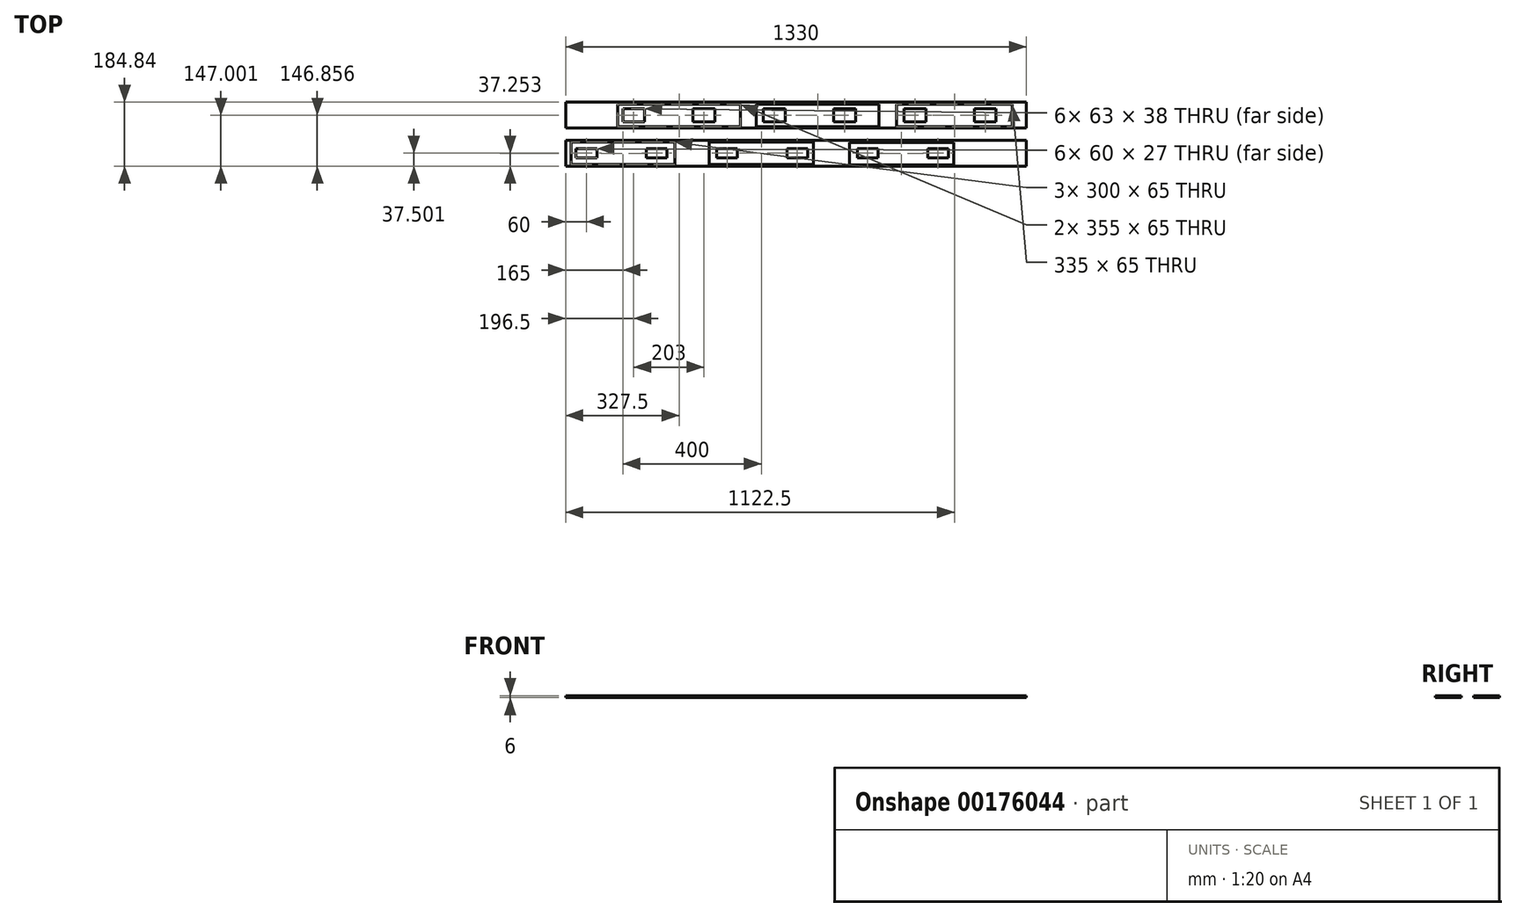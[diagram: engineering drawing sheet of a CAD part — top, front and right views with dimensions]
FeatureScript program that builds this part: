
annotation { "Feature Type Name" : "Feature", "Feature Type Description" : "" }
export const myFeature = defineFeature(function(context is Context, id is Id, definition is map)
    precondition{}
    {
        {
            var Q0;
            Q0=qCreatedBy(makeId("Top.planeOp"),FACE);
            var sketch = newSketch(context, id + "F0", { "sketchPlane" : qUnion([Q0])});
            skLineSegment(sketch, "E0.bottom", {"start": v(0, 0) * mm, "end": v(1330, 0) * mm});
            skLineSegment(sketch, "E0.top", {"start": v(0, 75) * mm, "end": v(1330, 75) * mm});
            skLineSegment(sketch, "E0.left", {"start": v(0, 0) * mm, "end": v(0, 75) * mm});
            skLineSegment(sketch, "E0.right", {"start": v(1330, 0) * mm, "end": v(1330, 75) * mm});
            skLineSegment(sketch, "E1.bottom", {"start": v(0, -34.84) * mm, "end": v(1330, -34.84) * mm});
            skLineSegment(sketch, "E1.top", {"start": v(0, -109.84) * mm, "end": v(1330, -109.84) * mm});
            skLineSegment(sketch, "E1.left", {"start": v(0, -34.84) * mm, "end": v(0, -109.84) * mm});
            skLineSegment(sketch, "E1.right", {"start": v(1330, -34.84) * mm, "end": v(1330, -109.84) * mm});
            skLineSegment(sketch, "E2.bottom", {"start": v(15, -40.09) * mm, "end": v(315, -40.09) * mm});
            skLineSegment(sketch, "E2.top", {"start": v(15, -105.09) * mm, "end": v(315, -105.09) * mm});
            skLineSegment(sketch, "E2.left", {"start": v(15, -40.09) * mm, "end": v(15, -105.09) * mm});
            skLineSegment(sketch, "E2.right", {"start": v(315, -40.09) * mm, "end": v(315, -105.09) * mm});
            skLineSegment(sketch, "E3.bottom", {"start": v(415, -39.91) * mm, "end": v(715, -39.91) * mm});
            skLineSegment(sketch, "E3.top", {"start": v(415, -104.91) * mm, "end": v(715, -104.91) * mm});
            skLineSegment(sketch, "E3.left", {"start": v(415, -39.91) * mm, "end": v(415, -104.91) * mm});
            skLineSegment(sketch, "E3.right", {"start": v(715, -39.91) * mm, "end": v(715, -104.91) * mm});
            skLineSegment(sketch, "E4.bottom", {"start": v(820, -40.85) * mm, "end": v(1120, -40.85) * mm});
            skLineSegment(sketch, "E4.top", {"start": v(820, -105.85) * mm, "end": v(1120, -105.85) * mm});
            skLineSegment(sketch, "E4.left", {"start": v(820, -40.85) * mm, "end": v(820, -105.85) * mm});
            skLineSegment(sketch, "E4.right", {"start": v(1120, -40.85) * mm, "end": v(1120, -105.85) * mm});
            skLineSegment(sketch, "E5.bottom", {"start": v(150, 69.52) * mm, "end": v(505, 69.52) * mm});
            skLineSegment(sketch, "E5.top", {"start": v(150, 4.52) * mm, "end": v(505, 4.52) * mm});
            skLineSegment(sketch, "E5.left", {"start": v(150, 69.52) * mm, "end": v(150, 4.52) * mm});
            skLineSegment(sketch, "E5.right", {"start": v(505, 69.52) * mm, "end": v(505, 4.52) * mm});
            skLineSegment(sketch, "E6.bottom", {"start": v(550, 69.52) * mm, "end": v(905, 69.52) * mm});
            skLineSegment(sketch, "E6.top", {"start": v(550, 4.52) * mm, "end": v(905, 4.52) * mm});
            skLineSegment(sketch, "E6.left", {"start": v(550, 69.52) * mm, "end": v(550, 4.52) * mm});
            skLineSegment(sketch, "E6.right", {"start": v(905, 69.52) * mm, "end": v(905, 4.52) * mm});
            skLineSegment(sketch, "E7.bottom", {"start": v(955, 69.52) * mm, "end": v(1290, 69.52) * mm});
            skLineSegment(sketch, "E7.top", {"start": v(955, 4.52) * mm, "end": v(1290, 4.52) * mm});
            skLineSegment(sketch, "E7.left", {"start": v(955, 69.52) * mm, "end": v(955, 4.52) * mm});
            skLineSegment(sketch, "E7.right", {"start": v(1290, 69.52) * mm, "end": v(1290, 4.52) * mm});
            skSolve(sketch);
        }
        {
            var Q0;
            Q0=qCreatedBy(makeId("Top.planeOp"),FACE);
            var sketch = newSketch(context, id + "F1", { "sketchPlane" : qUnion([Q0])});
            skLineSegment(sketch, "E8.bottom", {"start": v(165, 56.16) * mm, "end": v(228, 56.16) * mm});
            skLineSegment(sketch, "E8.top", {"start": v(165, 18.16) * mm, "end": v(228, 18.16) * mm});
            skLineSegment(sketch, "E8.left", {"start": v(165, 56.16) * mm, "end": v(165, 18.16) * mm});
            skLineSegment(sketch, "E8.right", {"start": v(228, 56.16) * mm, "end": v(228, 18.16) * mm});
            skLineSegment(sketch, "E9.bottom", {"start": v(30, -58.84) * mm, "end": v(90, -58.84) * mm});
            skLineSegment(sketch, "E9.top", {"start": v(30, -85.84) * mm, "end": v(90, -85.84) * mm});
            skLineSegment(sketch, "E9.left", {"start": v(30, -58.84) * mm, "end": v(30, -85.84) * mm});
            skLineSegment(sketch, "E9.right", {"start": v(90, -58.84) * mm, "end": v(90, -85.84) * mm});
            skLineSegment(sketch, "E10.bottom", {"start": v(368, 56.16) * mm, "end": v(431, 56.16) * mm});
            skLineSegment(sketch, "E10.top", {"start": v(368, 18.16) * mm, "end": v(431, 18.16) * mm});
            skLineSegment(sketch, "E10.left", {"start": v(368, 56.16) * mm, "end": v(368, 18.16) * mm});
            skLineSegment(sketch, "E10.right", {"start": v(431, 56.16) * mm, "end": v(431, 18.16) * mm});
            skLineSegment(sketch, "E11.bottom", {"start": v(233, -58.84) * mm, "end": v(293, -58.84) * mm});
            skLineSegment(sketch, "E11.top", {"start": v(233, -85.84) * mm, "end": v(293, -85.84) * mm});
            skLineSegment(sketch, "E11.left", {"start": v(233, -58.84) * mm, "end": v(233, -85.84) * mm});
            skLineSegment(sketch, "E11.right", {"start": v(293, -58.84) * mm, "end": v(293, -85.84) * mm});
            skLineSegment(sketch, "E12.bottom", {"start": v(571, 56.16) * mm, "end": v(634, 56.16) * mm});
            skLineSegment(sketch, "E12.top", {"start": v(571, 18.16) * mm, "end": v(634, 18.16) * mm});
            skLineSegment(sketch, "E12.left", {"start": v(571, 56.16) * mm, "end": v(571, 18.16) * mm});
            skLineSegment(sketch, "E12.right", {"start": v(634, 56.16) * mm, "end": v(634, 18.16) * mm});
            skLineSegment(sketch, "E13.bottom", {"start": v(436, -58.84) * mm, "end": v(496, -58.84) * mm});
            skLineSegment(sketch, "E13.top", {"start": v(436, -85.84) * mm, "end": v(496, -85.84) * mm});
            skLineSegment(sketch, "E13.left", {"start": v(436, -58.84) * mm, "end": v(436, -85.84) * mm});
            skLineSegment(sketch, "E13.right", {"start": v(496, -58.84) * mm, "end": v(496, -85.84) * mm});
            skLineSegment(sketch, "E14.bottom", {"start": v(774, 56.16) * mm, "end": v(837, 56.16) * mm});
            skLineSegment(sketch, "E14.top", {"start": v(774, 18.16) * mm, "end": v(837, 18.16) * mm});
            skLineSegment(sketch, "E14.left", {"start": v(774, 56.16) * mm, "end": v(774, 18.16) * mm});
            skLineSegment(sketch, "E14.right", {"start": v(837, 56.16) * mm, "end": v(837, 18.16) * mm});
            skLineSegment(sketch, "E15.bottom", {"start": v(639, -58.84) * mm, "end": v(699, -58.84) * mm});
            skLineSegment(sketch, "E15.top", {"start": v(639, -85.84) * mm, "end": v(699, -85.84) * mm});
            skLineSegment(sketch, "E15.left", {"start": v(639, -58.84) * mm, "end": v(639, -85.84) * mm});
            skLineSegment(sketch, "E15.right", {"start": v(699, -58.84) * mm, "end": v(699, -85.84) * mm});
            skLineSegment(sketch, "E16.bottom", {"start": v(977, 56.16) * mm, "end": v(1040, 56.16) * mm});
            skLineSegment(sketch, "E16.top", {"start": v(977, 18.16) * mm, "end": v(1040, 18.16) * mm});
            skLineSegment(sketch, "E16.left", {"start": v(977, 56.16) * mm, "end": v(977, 18.16) * mm});
            skLineSegment(sketch, "E16.right", {"start": v(1040, 56.16) * mm, "end": v(1040, 18.16) * mm});
            skLineSegment(sketch, "E17.bottom", {"start": v(842, -58.84) * mm, "end": v(902, -58.84) * mm});
            skLineSegment(sketch, "E17.top", {"start": v(842, -85.84) * mm, "end": v(902, -85.84) * mm});
            skLineSegment(sketch, "E17.left", {"start": v(842, -58.84) * mm, "end": v(842, -85.84) * mm});
            skLineSegment(sketch, "E17.right", {"start": v(902, -58.84) * mm, "end": v(902, -85.84) * mm});
            skLineSegment(sketch, "E18.bottom", {"start": v(1180, 56.16) * mm, "end": v(1243, 56.16) * mm});
            skLineSegment(sketch, "E18.top", {"start": v(1180, 18.16) * mm, "end": v(1243, 18.16) * mm});
            skLineSegment(sketch, "E18.left", {"start": v(1180, 56.16) * mm, "end": v(1180, 18.16) * mm});
            skLineSegment(sketch, "E18.right", {"start": v(1243, 56.16) * mm, "end": v(1243, 18.16) * mm});
            skLineSegment(sketch, "E19.bottom", {"start": v(1045, -58.84) * mm, "end": v(1105, -58.84) * mm});
            skLineSegment(sketch, "E19.top", {"start": v(1045, -85.84) * mm, "end": v(1105, -85.84) * mm});
            skLineSegment(sketch, "E19.left", {"start": v(1045, -58.84) * mm, "end": v(1045, -85.84) * mm});
            skLineSegment(sketch, "E19.right", {"start": v(1105, -58.84) * mm, "end": v(1105, -85.84) * mm});
            skLineSegment(sketch, "E20.bottom", {"start": v(0, 0) * mm, "end": v(1330, 0) * mm});
            skLineSegment(sketch, "E20.top", {"start": v(0, 75) * mm, "end": v(1330, 75) * mm});
            skLineSegment(sketch, "E20.left", {"start": v(0, 0) * mm, "end": v(0, 75) * mm});
            skLineSegment(sketch, "E20.right", {"start": v(1330, 0) * mm, "end": v(1330, 75) * mm});
            skLineSegment(sketch, "E21.bottom", {"start": v(0, -34.84) * mm, "end": v(1330, -34.84) * mm});
            skLineSegment(sketch, "E21.top", {"start": v(0, -109.84) * mm, "end": v(1330, -109.84) * mm});
            skLineSegment(sketch, "E21.left", {"start": v(0, -34.84) * mm, "end": v(0, -109.84) * mm});
            skLineSegment(sketch, "E21.right", {"start": v(1330, -34.84) * mm, "end": v(1330, -109.84) * mm});
            skSolve(sketch);
        }
        {
            var Q0;
            Q0=makeQuery(id+"F0.imprint","IMPRINT",FACE,{"disambiguationData":[TD([[makeQuery(id+"F0.imprint","IMPRINT",EDGE,{"derivedFrom":sQuery(id+"F0.wireOp",EDGE,"E0.bottom")}),1.0]])]});
            var Q1;
            Q1=makeQuery(id+"F0.imprint","IMPRINT",FACE,{"disambiguationData":[TD([[makeQuery(id+"F0.imprint","IMPRINT",EDGE,{"derivedFrom":sQuery(id+"F0.wireOp",EDGE,"E1.bottom")}),-1.0]])]});
            extrude(context, id + "F2", {"entities" : qUnion([Q0, Q1]), "depth" : 3 * mm});
        }
        {
            var Q0;
            Q0 = qSketchRegion(id + "F1", true);
            extrude(context, id + "F3", {"entities" : qUnion([Q0]), "oppositeDirection" : true, "depth" : 3 * mm});
        }
    });
